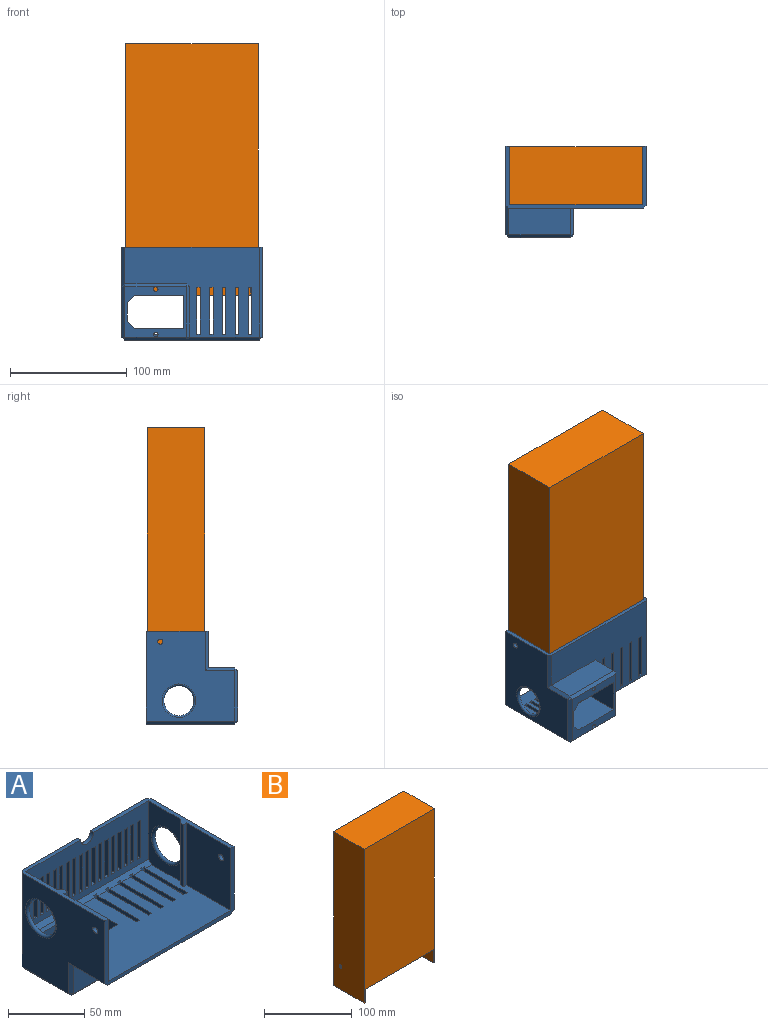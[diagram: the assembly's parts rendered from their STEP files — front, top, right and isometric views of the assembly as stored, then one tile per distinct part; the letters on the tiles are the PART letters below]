
ASSEMBLY  parts=2 mates=1
PART A: 146 faces, bbox 120.3x79.8x78.3 mm
  f0: plane 114x73.5mm, normal (0,0,1), area 6427.6mm2, adj f3,f6,f7,f9,f12,f13,f14,f15
  f1: plane 115x77mm, normal (0,0,-1), area 5719mm2, adj f9,f97,f98,f104,f105,f106,f107,f108
  f2: plane 114x47mm, normal (0,-1,0), area 3771.5mm2, adj f3,f4,f11,f12,f19,f20,f21,f22
  f3: plane 50x29.5mm, normal (1,0,0), area 844.4mm2, adj f0,f2,f11,f14,f144,f145
  f4: plane 79.5x54mm, normal (0,0,1), area 401.9mm2, adj f2,f5,f6,f9,f10,f12,f16,f17
  f5: plane 115x75.5mm, normal (0,1,0), area 5546mm2, adj f4,f11,f19,f20,f21,f22,f23,f24
  f6: plane 50x41mm, normal (-1,0,0), area 2034.1mm2, adj f0,f4,f9,f16,f90
  f7: plane 50x41mm, normal (1,0,0), area 2034.1mm2, adj f0,f9,f11,f15,f88
  f8: plane 77x75.5mm, normal (-1,0,0), area 4310.8mm2, adj f9,f11,f88,f124,f125,f127,f128,f144
  f9: plane 120x53mm, normal (0,-1,0), area 653.7mm2, adj f0,f1,f4,f6,f7,f8,f10,f11
  f10: plane 77x50.5mm, normal (1,0,0), area 3229.5mm2, adj f4,f9,f90,f137,f140,f142
  f11: plane 79.5x54mm, normal (0,0,1), area 401.9mm2, adj f2,f3,f5,f7,f8,f9,f13,f14
  f12: plane 50x29.5mm, normal (-1,0,0), area 844.4mm2, adj f0,f2,f4,f18,f142,f145
  f13: plane 50x3mm, normal (1,0,0), area 150mm2, adj f0,f11,f14,f15
  f14: plane 50.3x3.66mm, normal (0.71,0.71,0), area 206.5mm2, adj f0,f3,f11,f13,f143,f144
  f15: plane 50x3mm, normal (0,-1,0), area 150mm2, adj f0,f7,f11,f13
  f16: plane 50x3mm, normal (0,-1,0), area 150mm2, adj f0,f4,f6,f17
  f17: plane 50x3mm, normal (-1,0,0), area 150mm2, adj f0,f4,f16,f18
  f18: plane 50.3x3.66mm, normal (-0.71,0.71,0), area 206.5mm2, adj f0,f4,f12,f17,f141,f142
  f19: plane 3x3mm, normal (0,0,-1), area 9mm2, adj f2,f5,f20,f22
  f20: plane 30x3mm, normal (-1,0,0), area 90mm2, adj f2,f5,f19,f21
  f21: plane 3x3mm, normal (0,0,1), area 9mm2, adj f2,f5,f20,f22
  f22: plane 30x3mm, normal (1,0,0), area 90mm2, adj f2,f5,f19,f21
  f23: plane 3x3mm, normal (0,0,-1), area 9mm2, adj f2,f5,f24,f26
  f24: plane 30x3mm, normal (-1,0,0), area 90mm2, adj f2,f5,f23,f25
  f25: plane 3x3mm, normal (0,0,1), area 9mm2, adj f2,f5,f24,f26
  f26: plane 30x3mm, normal (1,0,0), area 90mm2, adj f2,f5,f23,f25
  f27: plane 3x3mm, normal (0,0,-1), area 9mm2, adj f2,f5,f28,f30
  f28: plane 30x3mm, normal (-1,0,0), area 90mm2, adj f2,f5,f27,f29
  f29: plane 3x3mm, normal (0,0,1), area 9mm2, adj f2,f5,f28,f30
  f30: plane 30x3mm, normal (1,0,0), area 90mm2, adj f2,f5,f27,f29
  f31: plane 3x3mm, normal (0,0,-1), area 9mm2, adj f2,f5,f32,f34
  f32: plane 30x3mm, normal (-1,0,0), area 90mm2, adj f2,f5,f31,f33
  f33: plane 3x3mm, normal (0,0,1), area 9mm2, adj f2,f5,f32,f34
  f34: plane 30x3mm, normal (1,0,0), area 90mm2, adj f2,f5,f31,f33
  f35: plane 3x3mm, normal (0,0,-1), area 9mm2, adj f2,f5,f36,f38
  f36: plane 30x3mm, normal (-1,0,0), area 90mm2, adj f2,f5,f35,f37
  f37: plane 3x3mm, normal (0,0,1), area 9mm2, adj f2,f5,f36,f38
  f38: plane 30x3mm, normal (1,0,0), area 90mm2, adj f2,f5,f35,f37
  f39: plane 3x3mm, normal (0,0,-1), area 9mm2, adj f2,f5,f40,f42
  f40: plane 30x3mm, normal (-1,0,0), area 90mm2, adj f2,f5,f39,f41
  f41: plane 3x3mm, normal (0,0,1), area 9mm2, adj f2,f5,f40,f42
  f42: plane 30x3mm, normal (1,0,0), area 90mm2, adj f2,f5,f39,f41
  f43: plane 3x3mm, normal (0,0,-1), area 9mm2, adj f2,f5,f44,f46
  f44: plane 30x3mm, normal (-1,0,0), area 90mm2, adj f2,f5,f43,f45
  f45: plane 3x3mm, normal (0,0,1), area 9mm2, adj f2,f5,f44,f46
  f46: plane 30x3mm, normal (1,0,0), area 90mm2, adj f2,f5,f43,f45
  f47: plane 3x3mm, normal (0,0,-1), area 9mm2, adj f2,f5,f48,f50
  f48: plane 30x3mm, normal (-1,0,0), area 90mm2, adj f2,f5,f47,f49
  f49: plane 3x3mm, normal (0,0,1), area 9mm2, adj f2,f5,f48,f50
  f50: plane 30x3mm, normal (1,0,0), area 90mm2, adj f2,f5,f47,f49
  f51: plane 3x3mm, normal (0,0,-1), area 9mm2, adj f2,f5,f52,f54
  f52: plane 30x3mm, normal (-1,0,0), area 90mm2, adj f2,f5,f51,f53
  f53: plane 3x3mm, normal (0,0,1), area 9mm2, adj f2,f5,f52,f54
  f54: plane 30x3mm, normal (1,0,0), area 90mm2, adj f2,f5,f51,f53
  f55: plane 3x3mm, normal (0,0,-1), area 9mm2, adj f2,f5,f56,f58
  f56: plane 30x3mm, normal (-1,0,0), area 90mm2, adj f2,f5,f55,f57
  f57: plane 3x3mm, normal (0,0,1), area 9mm2, adj f2,f5,f56,f58
  f58: plane 30x3mm, normal (1,0,0), area 90mm2, adj f2,f5,f55,f57
  f59: plane 3x3mm, normal (0,0,-1), area 9mm2, adj f2,f5,f60,f62
  f60: plane 30x3mm, normal (-1,0,0), area 90mm2, adj f2,f5,f59,f61
  f61: plane 3x3mm, normal (0,0,1), area 9mm2, adj f2,f5,f60,f62
  f62: plane 30x3mm, normal (1,0,0), area 90mm2, adj f2,f5,f59,f61
  f63: plane 3x3mm, normal (0,0,-1), area 9mm2, adj f2,f5,f64,f66
  f64: plane 30x3mm, normal (-1,0,0), area 90mm2, adj f2,f5,f63,f65
  f65: plane 3x3mm, normal (0,0,1), area 9mm2, adj f2,f5,f64,f66
  f66: plane 30x3mm, normal (1,0,0), area 90mm2, adj f2,f5,f63,f65
  f67: plane 3x3mm, normal (0,0,-1), area 9mm2, adj f2,f5,f68,f70
  f68: plane 30x3mm, normal (-1,0,0), area 90mm2, adj f2,f5,f67,f69
  f69: plane 3x3mm, normal (0,0,1), area 9mm2, adj f2,f5,f68,f70
  f70: plane 30x3mm, normal (1,0,0), area 90mm2, adj f2,f5,f67,f69
  f71: plane 3x3mm, normal (0,0,-1), area 9mm2, adj f2,f5,f72,f74
  f72: plane 30x3mm, normal (-1,0,0), area 90mm2, adj f2,f5,f71,f73
  f73: plane 3x3mm, normal (0,0,1), area 9mm2, adj f2,f5,f72,f74
  f74: plane 30x3mm, normal (1,0,0), area 90mm2, adj f2,f5,f71,f73
  f75: plane 3x3mm, normal (0,0,-1), area 9mm2, adj f2,f5,f76,f78
  f76: plane 30x3mm, normal (-1,0,0), area 90mm2, adj f2,f5,f75,f77
  f77: plane 3x3mm, normal (0,0,1), area 9mm2, adj f2,f5,f76,f78
  f78: plane 30x3mm, normal (1,0,0), area 90mm2, adj f2,f5,f75,f77
  f79: plane 3x3mm, normal (0,0,-1), area 9mm2, adj f2,f5,f80,f82
  f80: plane 30x3mm, normal (-1,0,0), area 90mm2, adj f2,f5,f79,f81
  f81: plane 3x3mm, normal (0,0,1), area 9mm2, adj f2,f5,f80,f82
  f82: plane 30x3mm, normal (1,0,0), area 90mm2, adj f2,f5,f79,f81
  f83: plane 3x3mm, normal (0,0,-1), area 9mm2, adj f2,f5,f84,f86
  f84: plane 30x3mm, normal (-1,0,0), area 90mm2, adj f2,f5,f83,f85
  f85: plane 3x3mm, normal (0,0,1), area 9mm2, adj f2,f5,f84,f86
  f86: plane 30x3mm, normal (1,0,0), area 90mm2, adj f2,f5,f83,f85
  f87: cylinder r=6mm len=12mm, axis (0,1,0), area 56.5mm2, adj f2,f4,f5,f11
  f88: cylinder r=2.25mm len=4.5mm, axis (1,0,0), area 42.4mm2, adj f7,f8
  f89: cylinder r=12.81mm len=10.21mm, axis (1,0,0), area 0mm2, adj f143,f144
  f90: cylinder r=2.25mm len=4.5mm, axis (-1,0,0), area 42.4mm2, adj f6,f10
  f91: cylinder r=12.81mm len=10.21mm, axis (-1,0,0), area 0mm2, adj f141,f142
  f92: plane 42.25x28mm, normal (0,1,0), area 1183mm2, adj f0,f93,f101,f102
  f93: plane 28.25x28mm, normal (-1,0,0), area 791mm2, adj f0,f92,f94,f102
  f94: plane 42.25x28mm, normal (0,-1,0), area 1183mm2, adj f0,f93,f95,f102
  f95: plane 28x6mm, normal (0.71,-0.71,0), area 237.6mm2, adj f0,f94,f96,f102
  f96: plane 28x16.25mm, normal (1,0,0), area 455mm2, adj f0,f95,f101,f102
  f97: plane 43.25x22.5mm, normal (1,0,0), area 973.1mm2, adj f1,f130,f134,f136
  f98: plane 53x22.5mm, normal (0,-1,0), area 1192.5mm2, adj f1,f125,f129,f130
  f99: cylinder r=1.9mm len=29mm, axis (0,0,1), area 342.1mm2, adj f0,f102,f103,f145
  f100: cylinder r=1.9mm len=28mm, axis (0,0,1), area 334.3mm2, adj f0,f102
  f101: plane 28x6mm, normal (0.71,0.71,0), area 237.6mm2, adj f0,f92,f96,f102
  f102: plane 53x43.25mm, normal (0,0,-1), area 942.5mm2, adj f92,f93,f94,f95,f96,f99,f100,f101
  f103: plane 3.8x2.28mm, normal (0,0,-1), area 7.1mm2, adj f99,f145
  f104: plane 40x4mm, normal (-1,0,0), area 120.5mm2, adj f0,f1,f105,f107,f145
  f105: plane 4x3mm, normal (0,-1,0), area 12mm2, adj f1,f104,f106,f145
  f106: plane 40x4mm, normal (1,0,0), area 120.5mm2, adj f0,f1,f105,f107,f145
  f107: plane 3x3mm, normal (0,1,0), area 9mm2, adj f0,f1,f104,f106
  f108: plane 40x4mm, normal (-1,0,0), area 120.5mm2, adj f0,f1,f109,f111,f145
  f109: plane 4x3mm, normal (0,-1,0), area 12mm2, adj f1,f108,f110,f145
  f110: plane 40x4mm, normal (1,0,0), area 120.5mm2, adj f0,f1,f109,f111,f145
  f111: plane 3x3mm, normal (0,1,0), area 9mm2, adj f0,f1,f108,f110
  f112: plane 40x4mm, normal (-1,0,0), area 120.5mm2, adj f0,f1,f113,f115,f145
  f113: plane 4x3mm, normal (0,-1,0), area 12mm2, adj f1,f112,f114,f145
  f114: plane 40x4mm, normal (1,0,0), area 120.5mm2, adj f0,f1,f113,f115,f145
  f115: plane 3x3mm, normal (0,1,0), area 9mm2, adj f0,f1,f112,f114
  f116: plane 40x4mm, normal (-1,0,0), area 120.5mm2, adj f0,f1,f117,f119,f145
  f117: plane 4x3mm, normal (0,-1,0), area 12mm2, adj f1,f116,f118,f145
  f118: plane 40x4mm, normal (1,0,0), area 120.5mm2, adj f0,f1,f117,f119,f145
  f119: plane 3x3mm, normal (0,1,0), area 9mm2, adj f0,f1,f116,f118
  f120: plane 40x4mm, normal (-1,0,0), area 120.5mm2, adj f0,f1,f121,f123,f145
  f121: plane 4x3mm, normal (0,-1,0), area 12mm2, adj f1,f120,f122,f145
  f122: plane 40x4mm, normal (1,0,0), area 120.5mm2, adj f0,f1,f121,f123,f145
  f123: plane 3x3mm, normal (0,1,0), area 9mm2, adj f0,f1,f120,f122
  f124: plane 33.75x2.5mm, normal (-0.71,0,-0.71), area 114.9mm2, adj f1,f8,f9,f125
  f125: plane 25x2.5mm, normal (-0.71,-0.71,0), area 84mm2, adj f8,f98,f124,f126
  f126: plane 2.5x2.5mm, normal (-0.58,-0.58,-0.58), area 5.4mm2, adj f125,f128,f129
  f127: plane 75.5x2.5mm, normal (-0.71,0.71,0), area 266.9mm2, adj f5,f8,f11,f131
  f128: plane 43.25x2.5mm, normal (-0.71,0,-0.71), area 152.9mm2, adj f8,f102,f126,f131
  f129: plane 53x2.5mm, normal (0,-0.71,-0.71), area 187.4mm2, adj f98,f102,f126,f132
  f130: plane 22.5x2.5mm, normal (0.71,-0.71,0), area 79.5mm2, adj f1,f97,f98,f132
  f131: plane 2.5x2.5mm, normal (-0.58,0.58,-0.58), area 5.4mm2, adj f127,f128,f133
  f132: plane 2.5x2.5mm, normal (0.58,-0.58,-0.58), area 5.4mm2, adj f129,f130,f134
  f133: plane 53x2.5mm, normal (0,0.71,-0.71), area 187.4mm2, adj f5,f102,f131,f135
  f134: plane 43.25x2.5mm, normal (0.71,0,-0.71), area 152.9mm2, adj f97,f102,f132,f135
  f135: plane 2.5x2.5mm, normal (0.58,0.58,-0.58), area 5.4mm2, adj f133,f134,f136
  f136: plane 25x2.5mm, normal (0.71,0.71,0), area 84mm2, adj f5,f97,f135,f138
  f137: plane 50.5x2.5mm, normal (0.71,0.71,0), area 178.5mm2, adj f4,f5,f10,f139
  f138: plane 62x2.5mm, normal (0,0.71,-0.71), area 214.8mm2, adj f1,f5,f136,f139
  f139: plane 2.5x2.5mm, normal (0.58,0.58,-0.58), area 5.4mm2, adj f137,f138,f140
  f140: plane 77x2.5mm, normal (0.71,0,-0.71), area 272.2mm2, adj f1,f9,f10,f139
  f141: bspline ~11.41x2.25mm, area 13.6mm2, adj f18,f91,f142
  f142: torus R=14.31mm, axis (-1,0,0), area 367.6mm2, adj f10,f12,f18,f91,f141
  f143: bspline ~11.41x2.25mm, area 13.6mm2, adj f14,f89,f144
  f144: torus R=14.31mm, axis (-1,0,0), area 367.6mm2, adj f3,f8,f14,f89,f143
  f145: plane 114.09x3.09mm, normal (0,-0.71,0.71), area 457.8mm2, adj f0,f2,f3,f12,f99,f103,f104,f105
PART B: 18 faces, bbox 113.5x49.4x215 mm
  f0: plane 110.5x18.4mm, normal (0,-1,0), area 685.7mm2, adj f6,f7,f8,f9,f10,f11,f12
  f1: plane 215x49.4mm, normal (-1,0,0), area 10605.1mm2, adj f2,f4,f5,f6,f16
  f2: plane 215x113.5mm, normal (0,-1,0), area 22369.3mm2, adj f1,f3,f5,f6,f7,f8,f9
  f3: plane 215x49.4mm, normal (1,0,0), area 10605.1mm2, adj f2,f4,f5,f6,f14
  f4: plane 215x113.5mm, normal (0,1,0), area 24402.5mm2, adj f1,f3,f5,f6
  f5: plane 113.5x49.4mm, normal (0,0,1), area 5606.9mm2, adj f1,f2,f3,f4
  f6: plane 113.5x49.4mm, normal (0,0,-1), area 2453.4mm2, adj f0,f1,f2,f3,f4,f7,f8,f10
  f7: plane 42x18.4mm, normal (1,0,0), area 772.8mm2, adj f0,f2,f6,f9
  f8: plane 42x18.4mm, normal (-1,0,0), area 772.8mm2, adj f0,f2,f6,f9
  f9: plane 110.5x42mm, normal (0,0,-1), area 4641mm2, adj f0,f2,f7,f8
  f10: plane 17x15.4mm, normal (1,0,0), area 261.8mm2, adj f0,f6,f11,f13
  f11: plane 87.5x17mm, normal (0,0,1), area 1487.5mm2, adj f0,f10,f12,f13
  f12: plane 17x15.4mm, normal (-1,0,0), area 261.8mm2, adj f0,f6,f11,f13
  f13: plane 87.5x15.4mm, normal (0,-1,0), area 1347.5mm2, adj f6,f10,f11,f12
  f14: cylinder r=2.25mm len=4.5mm, axis (1,0,0), area 21.2mm2, adj f3,f15
  f15: plane 4.5x4.5mm, normal (1,0,0), area 15.9mm2, adj f14
  f16: cylinder r=2.25mm len=4.5mm, axis (-1,0,0), area 21.2mm2, adj f1,f17
  f17: plane 4.5x4.5mm, normal (-1,0,0), area 15.9mm2, adj f16
PLACE A rot(axis=(-1,0,0),90deg) t=(54.99,-6.5,-9.62)mm
PLACE B t=(-1.76,-3.5,-10.87)mm
MATE fastened B.f14 <-> A.f88  axis (-1,0,0) through (-1.76,34.6,21.13)mm
